# Revit family: hewi_rail_with_shower_head_holder_801_33_110
name_source: partatom
category: Generic Models
revit_build: Autodesk Revit 2015 (Build: 20140903_1530(x64)
units: mm (PartAtom-declared; Revit-internal decimal feet)

## types (1)
- hewi_rail_with_shower_head_holder_801_33_110
    BIMobject category = Accessories
    BOSUseNativeGeometries = 1
    Brand url = http://www.hewi.com
    Design country = Germany
    Edition number = 1
    IFC Classification = Furnishing Element
    Installation instructions = https://catalog.hewi.com
    Manufacturer country = Germany
    Manufacturer name = HEWI
    Masterformat 2014 Code = 12 44 00
    Masterformat 2014 Description = Bath Furnishings
    Material main = Polyamide
    Material secondary = Steel
    NBS Reference Code = 31-75
    NBS Reference Description = Sanitary Accessories
    Nominal height = 0
    Nominal width = 33
    OmniClass Code = 23-19 31 17
    OmniClass Description = Sanitary Room Units
    Product Guid = 3bf85323-9647-41bc-b3ba-68c30534e6ee
    Product SKU = 801-33-110
    Product data url = https://bimobject.com
    Product family = Accessibility
    Product group = Shower holders
    Product name = HEWI Rail with shower head holder 801-33-110
    Product url = https://catalog.hewi.com
    QR code = http://bimobject.com
    Technical description = https://catalog.hewi.com
    UNSPSC Code = 301815
    Uniclass 1.4 Code = L721
    Uniclass 1.4 Description = Sanitary equipment
    Uniclass 2.0 Code = PR-31-75
    Uniclass 2.0 Description = Sanitary Accessories
    Uniclass 2015 Code = Pr_40_20_76
    Uniclass 2015 Name = Sanitary accessories
    Uniformat II Code = E20
    Uniformat II Description = FURNISHINGS
    Weight Net (Kg) = 0

## geometry (parser evidence)
native form markers: Sweep x1
no freeform markers — native parametric forms only
